# Revit family: Furniture-Mirrored_Cabinet-KOHLER-Verdera-K-99007
name_source: partatom
category: Specialty Equipment
revit_build: Autodesk Revit 2015 (Build: 20140606_1530(x64)
units: mm (PartAtom-declared; Revit-internal decimal feet)

## types (2) — shared parameters
ADA Compliant = No
Assembly Code = C1030200
Date Modified = 9/21/2018
Default Elevation = 42"
Finish = Kohler-Metal-NA-Anodized_Aluminum
Height = 30"
Manufacturer = KOHLER Co.
MasterFormat 1995 = 10820
MasterFormat 2004 = 10.28.13
Material = Anodized Aluminum Construction
Product Documentation Link = http://www.us.kohler.com
Product Name = Verdera
Product Page URL = http://www.us.kohler.com
URL = https://www.us.kohler.com
Width = 24"

## per-type parameters (varying)
| type | Description | Model | Type |
| NA-Anondized Aluminum | 24 inches W x 30 inches H aluminum medicine cabinet with adjustable magnifying mirror and slow-close door | K-99007-NA | 1 |
| Flip out mirror, NA-Anondized Aluminum | Aluminum medicine cabinet with adjustable flip-out flat mirror, 24 inches W x 30 inches H | K-99007-SCF-NA | 2 |

## geometry (parser evidence)
native form markers: Blend x2, Sweep x6
no freeform markers — native parametric forms only
